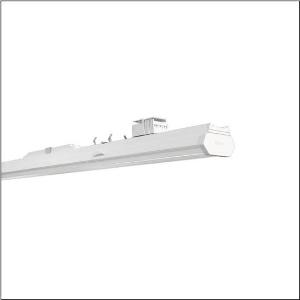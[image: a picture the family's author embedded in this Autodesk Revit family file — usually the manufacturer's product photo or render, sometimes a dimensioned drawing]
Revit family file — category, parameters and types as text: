
# Revit family: licross_r__11_protected_mo_51td12dn495g3s4_8e8e
name_source: partatom
category: Lighting Fixtures
units: mm (PartAtom-declared; Revit-internal decimal feet)

## family parameters
Cut with Voids When Loaded = No
Host = Face
Light Source = No
Part Type = Normal
Room Calculation Point = No
Round Connector Dimension = Use Diameter
Shared = No

## types (1)
- --- (1 x LED, 980 lm, 6.8 W, 4000K)
    Apparent Load = 7 VA
    CIE Flux Codes = 73 92 98 99 100
    Color Rendering = 80
    Color Temperature = 4000K
    Default Elevation = 1800 mm
    Description = Licross® 11 Protected MO, luminaire insert, of sheet steel, galvanised, coil coated, white, length: 1.500mm, width: 90mm, height: 101mm, LED rated luminous flux: 9.980lm, light colour: 840, control gear: DALI 2, with plug, 6-pole, with phase selection, for trunking rail, 9 or 11-core, mains connection: 220..240V, AC, 50/60Hz, rated input power: 61W, for trunking rail, 9-/11-core, halogen-free wiring, for emergency light function, converter,control gear: single battery element, battery: LiFePO4, 9Ah, primary light control with lens, of plastic, primary optical cover: cover, of PMMA, light emission: direct distribution, primary light characteristic: symmetric, protection rating (complete): IP54, insulation class (complete): insulation class I (protective earthing), certification: CE, UKCA, protection symbol: D if used in an environment with non-conductive dust loads with corresponding accessories, impact resistance: IK06, permissible ambient temperature for indoor applications: +5..+35°C, standard: EN 60598-2-22, LABS conformity tested according to VDMA 24364:2018-05, reducing of maximum allowable ambient temperature of 5°C with ceiling mounting, corresponds to IFS (International Featured Standards) requirements for safety and quality in the food industry, packaging unit: 1 piece
    Height = 92 mm
    Lamp = 1 x LED
    Lamp Light Flux = 980 lm
    Lamp Power = 6.8 W
    Lamp count = 1
    Length = 1500 mm
    Luminous efficacy = 144 lm/W
    Manufacturer = Siteco
    ModVariant = No
    Model = 51TD12DN495G3S4
    Mounting Place = Ceiling
    Mounting Type = Pendant
    Number of Poles = 1
    OnlyDefault = Yes
    Power Factor = 1
    Product Name = Licross® 11 Protected MO
    Product group = luminaire insert
    ProductGroupID = 901
    Protection Class = Protection class I
    Protection Degree = IP 54
    RLX_Detail_Level = 1
    RLX_Emergency_Light_Flux = 0 lm
    RLX_Emergency_Type = 0
    RLX_Emergency_Type_DB = No
    RlxData = <blob elided: 24813 chars, md5=459df2f0>
    Socket = socket
    Standby Power = 0 W
    System Light Flux = 980 lm
    System Power = 7 W
    Type Comments = : emergency light operation: 3 h
    Type Image = l_1256145.jpg
    URL = http://relux.com
    VarID = @adj_059357
    Voltage = 0 V
    Weight = 0.00 kg
    Width = 88 mm

## geometry (parser evidence)
native form markers: Blend x4, Sweep x11
no freeform markers — native parametric forms only
